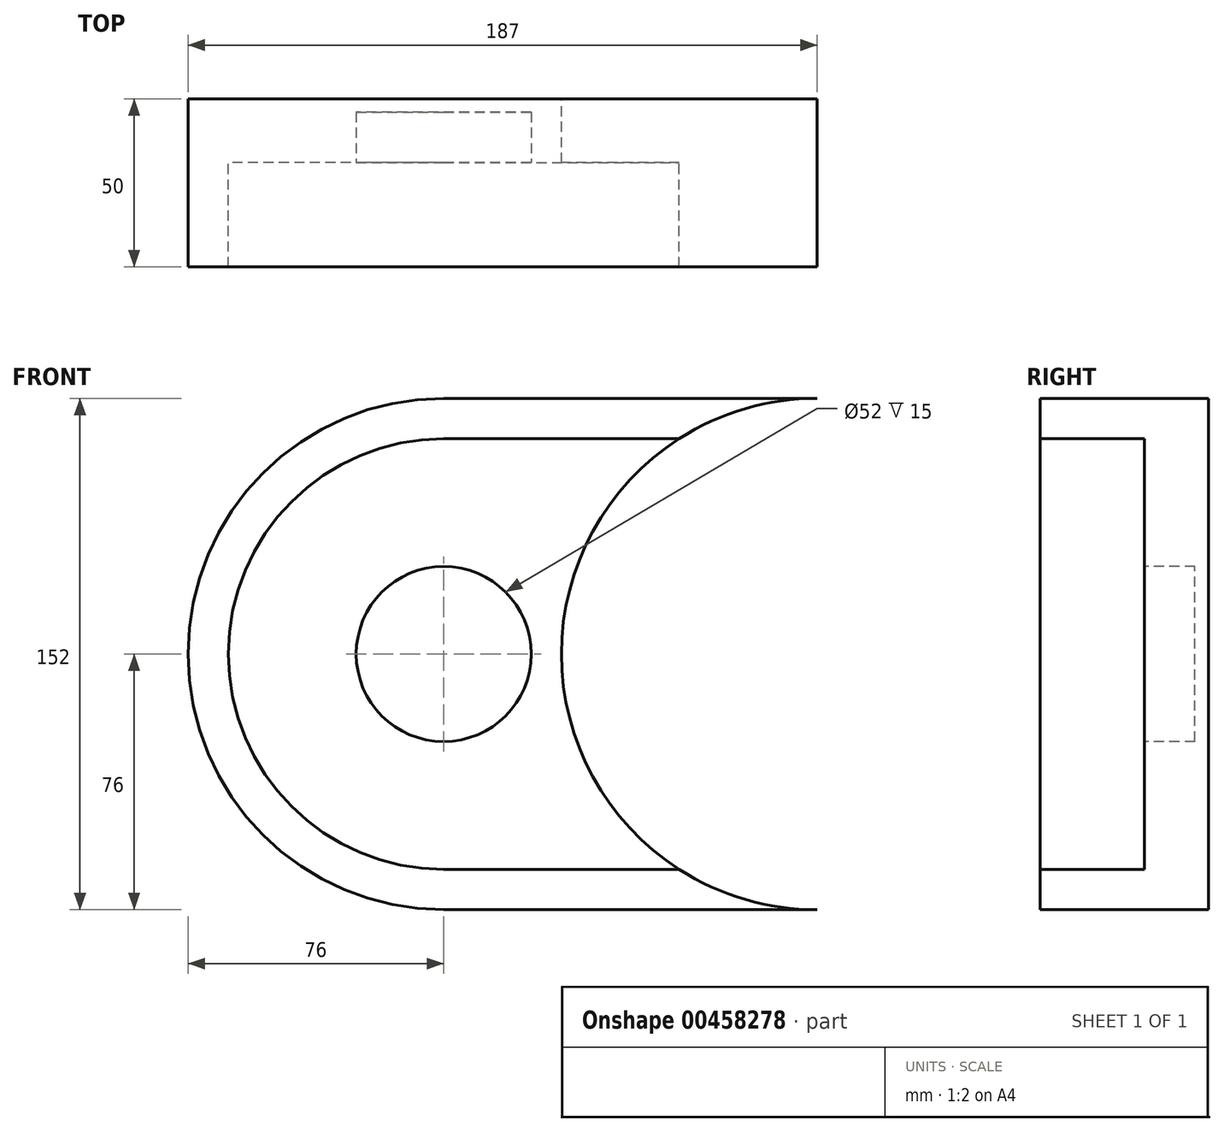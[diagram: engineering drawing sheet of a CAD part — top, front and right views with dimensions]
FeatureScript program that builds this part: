
annotation { "Feature Type Name" : "Feature", "Feature Type Description" : "" }
export const myFeature = defineFeature(function(context is Context, id is Id, definition is map)
    precondition{}
    {
        {
            var Q0;
            Q0=qCreatedBy(makeId("Front.planeOp"),FACE);
            var sketch = newSketch(context, id + "F0", { "sketchPlane" : qUnion([Q0])});
            skCircle(sketch, "E0", {"center": v(0, 0) * mm, "radius": 76 * mm});
            skCircle(sketch, "E1", {"center": v(111, 0) * mm, "radius": 76 * mm});
            skLineSegment(sketch, "E2", {"start": v(0, 76) * mm, "end": v(111, 76) * mm});
            skLineSegment(sketch, "E3", {"start": v(0, -76) * mm, "end": v(111, -76) * mm});
            skSolve(sketch);
        }
        {
            var Q0;
            {var subQ0=sQuery(id+"F0.wireOp",EDGE,"E0");var subQ1=makeQuery(id+"F0.imprint","INTERSECT",VERTEX,{"derivedFrom":[subQ0,sQuery(id+"F0.wireOp",EDGE,"E2")]});Q0=makeQuery(id+"F0.imprint","IMPRINT",FACE,{"disambiguationData":[TD([[makeQuery(id+"F0.imprint","IMPRINT",EDGE,{"disambiguationData":[TD([[subQ1,1.0]])],"derivedFrom":subQ0}),1.0]])]});}
            var Q1;
            {var subQ0=sQuery(id+"F0.wireOp",EDGE,"E1");var subQ1=sQuery(id+"F0.wireOp",EDGE,"E0");var subQ2=makeQuery(id+"F0.imprint","INTERSECT",VERTEX,{"disambiguationData":[OD(0.0)],"derivedFrom":[subQ1,subQ0]});Q1=makeQuery(id+"F0.imprint","IMPRINT",FACE,{"disambiguationData":[TD([[makeQuery(id+"F0.imprint","IMPRINT",EDGE,{"disambiguationData":[TD([[subQ2,1.0]])],"derivedFrom":subQ1}),-1.0]])]});}
            var Q2;
            {var subQ0=sQuery(id+"F0.wireOp",EDGE,"E1");var subQ1=sQuery(id+"F0.wireOp",EDGE,"E0");var subQ2=makeQuery(id+"F0.imprint","INTERSECT",VERTEX,{"disambiguationData":[OD(0.0)],"derivedFrom":[subQ1,subQ0]});Q2=makeQuery(id+"F0.imprint","IMPRINT",FACE,{"disambiguationData":[TD([[makeQuery(id+"F0.imprint","IMPRINT",EDGE,{"disambiguationData":[TD([[subQ2,1.0]])],"derivedFrom":subQ1}),1.0]])]});}
            var Q3;
            {var subQ0=sQuery(id+"F0.wireOp",EDGE,"E2");Q3=makeQuery(id+"F0.imprint","IMPRINT",FACE,{"disambiguationData":[TD([[makeQuery(id+"F0.imprint","IMPRINT",EDGE,{"derivedFrom":subQ0}),-1.0]])]});}
            var Q4;
            {var subQ0=sQuery(id+"F0.wireOp",EDGE,"E3");Q4=makeQuery(id+"F0.imprint","IMPRINT",FACE,{"disambiguationData":[TD([[makeQuery(id+"F0.imprint","IMPRINT",EDGE,{"derivedFrom":subQ0}),1.0]])]});}
            extrude(context, id + "F1", {"entities" : qUnion([Q0, Q1, Q2, Q3, Q4]), "depth" : 50 * mm, "offsetDistance" : 25 * mm});
        }
        {
            var Q0;
            Q0=qCreatedBy(makeId("Front.planeOp"),FACE);
            cPlane(context, id + "F2", {"entities" : qUnion([Q0]), "cplaneType" : CPlaneType.OFFSET, "offset" : 19 * mm, "width" : 150 * mm, "height" : 150 * mm});
        }
        {
            var Q0;
            Q0=qCreatedBy(id+"F2.planeOp",FACE);
            var sketch = newSketch(context, id + "F3", { "sketchPlane" : qUnion([Q0])});
            skArc(sketch, "E4", {"start": v(0, 64) * mm, "mid": v(-64, 0) * mm, "end": v(0, -64) * mm});
            skLineSegment(sketch, "E5", {"start": v(0, 0) * mm, "end": v(111, 0) * mm, "construction": true});
            skArc(sketch, "E6", {"start": v(111, -64) * mm, "mid": v(175, 0) * mm, "end": v(111, 64) * mm});
            skLineSegment(sketch, "E7", {"start": v(0, 64) * mm, "end": v(111, 64) * mm});
            skLineSegment(sketch, "E8", {"start": v(0, -64) * mm, "end": v(111, -64) * mm});
            skSolve(sketch);
        }
        {
            var Q0;
            Q0=makeQuery(id+"F3.imprint","IMPRINT",FACE,{"disambiguationData":[TD([[makeQuery(id+"F3.imprint","IMPRINT",EDGE,{"derivedFrom":sQuery(id+"F3.wireOp",EDGE,"E4")}),1.0]])]});
            extrude(context, id + "F4", {"entities" : qUnion([Q0]), "operationType" : NewBodyOperationType.REMOVE, "depth" : 31 * mm, "offsetDistance" : 25 * mm});
        }
        {
            var Q0;
            Q0=makeQuery(id+"F4.boolean.opBoolean","COPY",FACE,{"derivedFrom":makeQuery(id+"F4.opExtrude","CAP_FACE",FACE,{"disambiguationData":[OSD([sQuery(id+"F3.wireOp",EDGE,"E4"),sQuery(id+"F3.wireOp",EDGE,"E6"),sQuery(id+"F3.wireOp",EDGE,"E7"),sQuery(id+"F3.wireOp",EDGE,"E8")])],"isStart":true})});
            var sketch = newSketch(context, id + "F5", { "sketchPlane" : qUnion([Q0])});
            skCircle(sketch, "E9", {"center": v(0, 0) * mm, "radius": 26 * mm});
            skSolve(sketch);
        }
        {
            var Q0;
            Q0=makeQuery(id+"F5.imprint","IMPRINT",FACE,{"disambiguationData":[TD([[makeQuery(id+"F5.imprint","IMPRINT",EDGE,{"derivedFrom":sQuery(id+"F5.wireOp",EDGE,"E9")}),1.0]])]});
            extrude(context, id + "F6", {"entities" : qUnion([Q0]), "operationType" : NewBodyOperationType.REMOVE, "oppositeDirection" : true, "depth" : 15 * mm, "offsetDistance" : 25 * mm});
        }
        {
            var Q0;
            Q0=qCreatedBy(makeId("Right.planeOp"),FACE);
            cPlane(context, id + "F7", {"entities" : qUnion([Q0]), "cplaneType" : CPlaneType.OFFSET, "offset" : 111 * mm, "width" : 150 * mm, "height" : 150 * mm});
        }
        {
            var Q0;
            Q0=qCreatedBy(id+"F7.planeOp",FACE);
            var sketch = newSketch(context, id + "F8", { "sketchPlane" : qUnion([Q0])});
            skLineSegment(sketch, "E10", {"start": v(0, 0) * mm, "end": v(-19, 0) * mm});
            skLineSegment(sketch, "E11", {"start": v(-7, 23.5) * mm, "end": v(-19, 23.5) * mm, "construction": true});
            skLineSegment(sketch, "E12", {"start": v(-2, 18.5) * mm, "end": v(-7, 18.5) * mm, "construction": true});
            skLineSegment(sketch, "E13", {"start": v(0, 11) * mm, "end": v(-2, 11) * mm, "construction": true});
            skLineSegment(sketch, "E14", {"start": v(-19, 0) * mm, "end": v(-19, 23.5) * mm});
            skLineSegment(sketch, "E15", {"start": v(-19, 23.5) * mm, "end": v(-7, 23.5) * mm});
            skLineSegment(sketch, "E16", {"start": v(-7, 23.5) * mm, "end": v(-7, 18.5) * mm});
            skLineSegment(sketch, "E17", {"start": v(-7, 18.5) * mm, "end": v(-2, 18.5) * mm});
            skLineSegment(sketch, "E18", {"start": v(-2, 18.5) * mm, "end": v(-2, 11) * mm});
            skLineSegment(sketch, "E19", {"start": v(-2, 11) * mm, "end": v(0, 11) * mm});
            skLineSegment(sketch, "E20", {"start": v(0, 0) * mm, "end": v(-19, 0) * mm, "construction": true});
            skLineSegment(sketch, "E21", {"start": v(0, 11) * mm, "end": v(0, 0) * mm});
            skLineSegment(sketch, "E22", {"start": v(0, 0) * mm, "end": v(-62.53, 0) * mm, "construction": true});
            skSolve(sketch);
        }
        {
            var Q0;
            Q0 = qSketchRegion(id + "F8", true);
            var Q1;
            Q1=sQuery(id+"F8.wireOp",EDGE,"E22");
            revolve(context, id + "F9", {"operationType" : NewBodyOperationType.REMOVE, "entities" : qUnion([Q0]), "axis" : qUnion([Q1]), "revolveType" : RevolveType.FULL, "oppositeDirection" : true});
        }
    });
